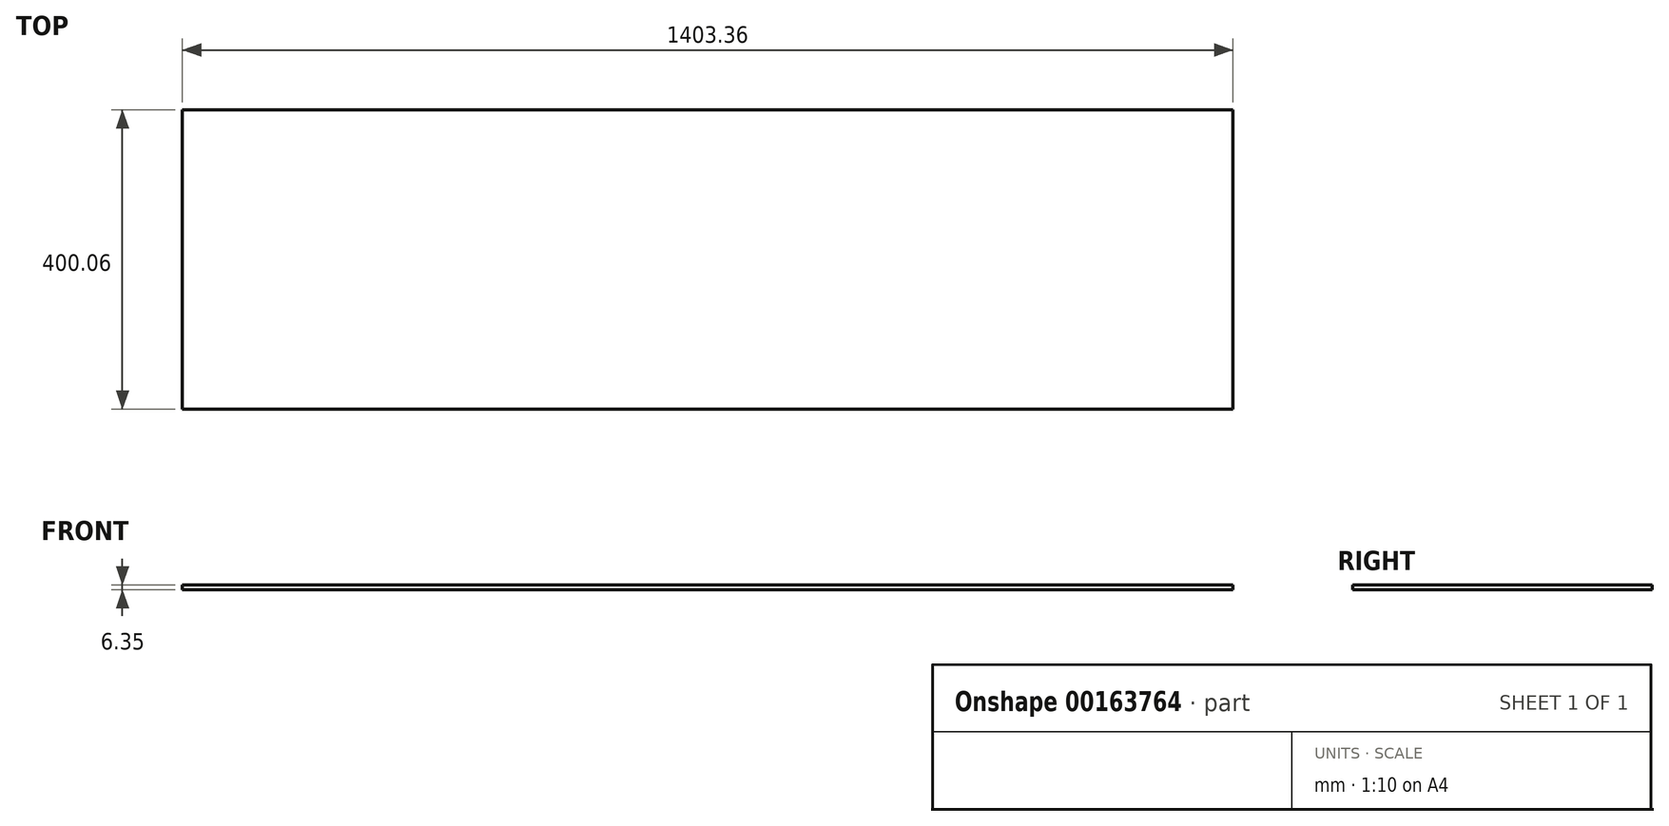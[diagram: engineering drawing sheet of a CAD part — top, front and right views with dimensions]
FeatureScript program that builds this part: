
annotation { "Feature Type Name" : "Feature", "Feature Type Description" : "" }
export const myFeature = defineFeature(function(context is Context, id is Id, definition is map)
    precondition{}
    {
        {
            var Q0;
            Q0=qCreatedBy(makeId("Top.planeOp"),FACE);
            var sketch = newSketch(context, id + "F0", { "sketchPlane" : qUnion([Q0])});
            skLineSegment(sketch, "E0.bottom", {"start": v(701.68, 200.03) * mm, "end": v(-701.68, 200.03) * mm});
            skLineSegment(sketch, "E0.top", {"start": v(701.68, -200.03) * mm, "end": v(-701.68, -200.03) * mm});
            skLineSegment(sketch, "E0.left", {"start": v(701.68, 200.03) * mm, "end": v(701.68, -200.03) * mm});
            skLineSegment(sketch, "E0.right", {"start": v(-701.68, 200.03) * mm, "end": v(-701.68, -200.03) * mm});
            skPoint(sketch, "E0.middle", {"position": v(0, 0) * mm});
            skSolve(sketch);
        }
        {
            var Q0;
            Q0 = qSketchRegion(id + "F0", true);
            extrude(context, id + "F1", {"entities" : qUnion([Q0]), "depth" : 6.35 * mm});
        }
    });
